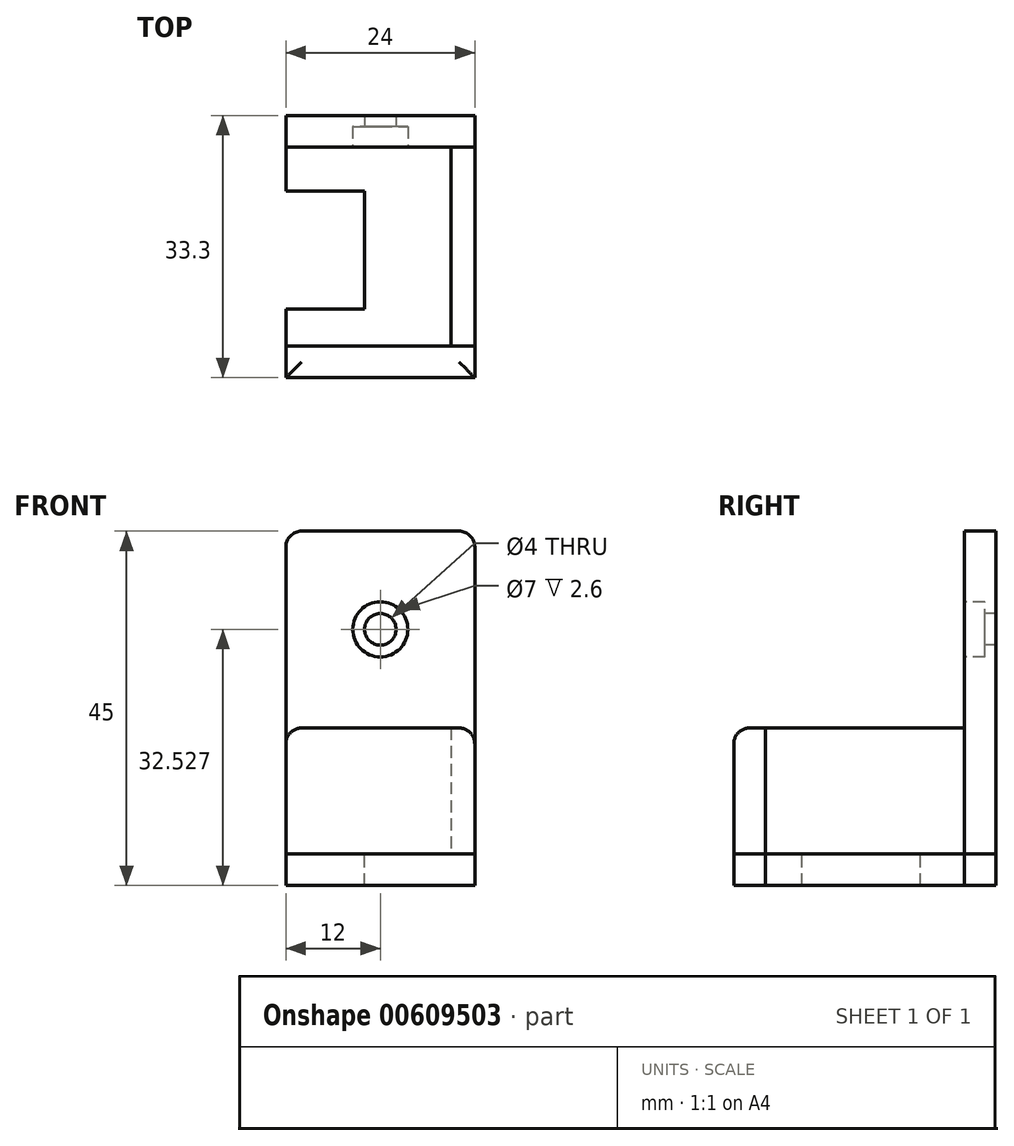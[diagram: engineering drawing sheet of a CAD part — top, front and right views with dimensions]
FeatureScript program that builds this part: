
annotation { "Feature Type Name" : "Feature", "Feature Type Description" : "" }
export const myFeature = defineFeature(function(context is Context, id is Id, definition is map)
    precondition{}
    {
        {
            var Q0;
            Q0=qCreatedBy(makeId("Top.planeOp"),FACE);
            var sketch = newSketch(context, id + "F0", { "sketchPlane" : qUnion([Q0])});
            skLineSegment(sketch, "E0.bottom", {"start": v(12, -16.65) * mm, "end": v(-12, -16.65) * mm});
            skLineSegment(sketch, "E0.top", {"start": v(12, 16.65) * mm, "end": v(-12, 16.65) * mm});
            skLineSegment(sketch, "E0.left", {"start": v(12, -16.65) * mm, "end": v(12, 16.65) * mm});
            skLineSegment(sketch, "E0.right", {"start": v(-12, -16.65) * mm, "end": v(-12, 16.65) * mm});
            skPoint(sketch, "E0.middle", {"position": v(0, 0) * mm});
            skSolve(sketch);
        }
        {
            var Q0;
            Q0=qSketchRegion(id+"F0",true);
            extrude(context, id + "F1", {"entities" : qUnion([Q0]), "depth" : 4 * mm, "offsetDistance" : 25 * mm});
        }
        {
            var Q0;
            Q0=makeQuery(id+"F0.imprint","IMPRINT",FACE,{"disambiguationData":[TD([[makeQuery(id+"F0.imprint","IMPRINT",EDGE,{"derivedFrom":sQuery(id+"F0.wireOp",EDGE,"E0.bottom")}),-1.0]])]});
            var sketch = newSketch(context, id + "F2", { "sketchPlane" : qUnion([Q0])});
            skLineSegment(sketch, "E1.bottom", {"start": v(-12, 16.65) * mm, "end": v(12, 16.65) * mm});
            skLineSegment(sketch, "E1.top", {"start": v(-12, 12.65) * mm, "end": v(12, 12.65) * mm});
            skLineSegment(sketch, "E1.left", {"start": v(-12, 16.65) * mm, "end": v(-12, 12.65) * mm});
            skLineSegment(sketch, "E1.right", {"start": v(12, 16.65) * mm, "end": v(12, 12.65) * mm});
            skSolve(sketch);
        }
        {
            var Q0;
            Q0=qSketchRegion(id+"F2",true);
            extrude(context, id + "F3", {"entities" : qUnion([Q0]), "depth" : 45 * mm, "offsetDistance" : 25 * mm});
        }
        {
            var Q0;
            Q0=makeQuery(id+"F2.imprint","IMPRINT",FACE,{"disambiguationData":[TD([[makeQuery(id+"F2.imprint","IMPRINT",EDGE,{"derivedFrom":sQuery(id+"F2.wireOp",EDGE,"E1.bottom")}),1.0]])]});
            var sketch = newSketch(context, id + "F4", { "sketchPlane" : qUnion([Q0])});
            skLineSegment(sketch, "E2.bottom", {"start": v(-12, -16.65) * mm, "end": v(12, -16.65) * mm});
            skLineSegment(sketch, "E2.top", {"start": v(-12, -12.65) * mm, "end": v(12, -12.65) * mm});
            skLineSegment(sketch, "E2.left", {"start": v(-12, -16.65) * mm, "end": v(-12, -12.65) * mm});
            skLineSegment(sketch, "E2.right", {"start": v(12, -16.65) * mm, "end": v(12, -12.65) * mm});
            skSolve(sketch);
        }
        {
            var Q0;
            Q0=qSketchRegion(id+"F4",true);
            extrude(context, id + "F5", {"entities" : qUnion([Q0]), "depth" : 20 * mm, "offsetDistance" : 25 * mm});
        }
        {
            var Q0;
            Q0=makeQuery(id+"F3.opExtrude","SWEPT_FACE",FACE,{"disambiguationData":[OSD([sQuery(id+"F2.wireOp",EDGE,"E1.top")])]});
            var sketch = newSketch(context, id + "F6", { "sketchPlane" : qUnion([Q0])});
            skCircle(sketch, "E3", {"center": v(0, 32.53) * mm, "radius": 2 * mm});
            skPoint(sketch, "E4", {"position": v(0, 40.1) * mm});
            skSolve(sketch);
        }
        {
            var Q0;
            Q0=qSketchRegion(id+"F6",true);
            extrude(context, id + "F7", {"entities" : qUnion([Q0]), "operationType" : NewBodyOperationType.REMOVE, "oppositeDirection" : true, "depth" : 6 * mm, "offsetDistance" : 25 * mm});
        }
        {
            var Q0;
            Q0=makeQuery(id+"F3.opExtrude","SWEPT_FACE",FACE,{"disambiguationData":[OSD([sQuery(id+"F2.wireOp",EDGE,"E1.top")])]});
            var sketch = newSketch(context, id + "F8", { "sketchPlane" : qUnion([Q0])});
            skCircle(sketch, "E5", {"center": v(0, 32.53) * mm, "radius": 3.5 * mm});
            skSolve(sketch);
        }
        {
            var Q0;
            Q0=qSketchRegion(id+"F8",true);
            extrude(context, id + "F9", {"entities" : qUnion([Q0]), "operationType" : NewBodyOperationType.REMOVE, "oppositeDirection" : true, "depth" : 2.6 * mm, "offsetDistance" : 25 * mm});
        }
        {
            var Q0;
            Q0=makeQuery(id+"F3.opExtrude","CAP_EDGE",EDGE,{"disambiguationData":[OSD([sQuery(id+"F2.wireOp",EDGE,"E1.left")])],"isStart":false});
            var Q1;
            Q1=makeQuery(id+"F3.opExtrude","CAP_EDGE",EDGE,{"disambiguationData":[OSD([sQuery(id+"F2.wireOp",EDGE,"E1.right")])],"isStart":false});
            fillet(context, id + "F10", {"entities" : qUnion([Q0, Q1]), "radius" : 2 * mm, "tangentPropagation" : true, "allowEdgeOverflow" : false});
        }
        {
            var Q0;
            Q0=makeQuery(id+"F1.opExtrude","CAP_FACE",FACE,{"disambiguationData":[OSD([sQuery(id+"F0.wireOp",EDGE,"E0.bottom"),sQuery(id+"F0.wireOp",EDGE,"E0.top"),sQuery(id+"F0.wireOp",EDGE,"E0.left"),sQuery(id+"F0.wireOp",EDGE,"E0.right")])],"isStart":false});
            var sketch = newSketch(context, id + "F11", { "sketchPlane" : qUnion([Q0])});
            skLineSegment(sketch, "E6.bottom", {"start": v(-17, 7.03) * mm, "end": v(-2, 7.03) * mm});
            skLineSegment(sketch, "E6.top", {"start": v(-17, -7.97) * mm, "end": v(-2, -7.97) * mm});
            skLineSegment(sketch, "E6.left", {"start": v(-17, 7.03) * mm, "end": v(-17, -7.97) * mm});
            skLineSegment(sketch, "E6.right", {"start": v(-2, 7.03) * mm, "end": v(-2, -7.97) * mm});
            skSolve(sketch);
        }
        {
            var Q0;
            Q0=makeQuery(id+"F1.opExtrude","CAP_FACE",FACE,{"disambiguationData":[OSD([sQuery(id+"F0.wireOp",EDGE,"E0.bottom"),sQuery(id+"F0.wireOp",EDGE,"E0.top"),sQuery(id+"F0.wireOp",EDGE,"E0.left"),sQuery(id+"F0.wireOp",EDGE,"E0.right")])],"isStart":false});
            var sketch = newSketch(context, id + "F12", { "sketchPlane" : qUnion([Q0])});
            skLineSegment(sketch, "E7.bottom", {"start": v(12, 12.65) * mm, "end": v(9, 12.65) * mm});
            skLineSegment(sketch, "E7.top", {"start": v(12, -12.65) * mm, "end": v(9, -12.65) * mm});
            skLineSegment(sketch, "E7.left", {"start": v(12, 12.65) * mm, "end": v(12, -12.65) * mm});
            skLineSegment(sketch, "E7.right", {"start": v(9, 12.65) * mm, "end": v(9, -12.65) * mm});
            skSolve(sketch);
        }
        {
            var Q0;
            Q0=makeQuery(id+"F12.imprint","IMPRINT",FACE,{"disambiguationData":[TD([[makeQuery(id+"F12.imprint","IMPRINT",EDGE,{"derivedFrom":sQuery(id+"F12.wireOp",EDGE,"E7.bottom")}),1.0]])]});
            extrude(context, id + "F13", {"entities" : qUnion([Q0]), "depth" : 16 * mm, "offsetDistance" : 25 * mm});
        }
        {
            var Q0;
            Q0=makeQuery(id+"F5.opExtrude","CAP_EDGE",EDGE,{"disambiguationData":[OSD([sQuery(id+"F4.wireOp",EDGE,"E2.bottom")])],"isStart":false});
            var Q1;
            Q1=makeQuery(id+"F5.opExtrude","CAP_EDGE",EDGE,{"disambiguationData":[OSD([sQuery(id+"F4.wireOp",EDGE,"E2.left")])],"isStart":false});
            var Q2;
            Q2=makeQuery(id+"F13.opExtrude","CAP_EDGE",EDGE,{"disambiguationData":[OSD([sQuery(id+"F12.wireOp",EDGE,"E7.left")])],"isStart":false});
            var Q3;
            Q3=makeQuery(id+"F5.opExtrude","CAP_EDGE",EDGE,{"disambiguationData":[OSD([sQuery(id+"F4.wireOp",EDGE,"E2.right")])],"isStart":false});
            fillet(context, id + "F14", {"entities" : qUnion([Q0, Q1, Q2, Q3]), "radius" : 2 * mm, "tangentPropagation" : true, "allowEdgeOverflow" : false});
        }
        {
            var Q0;
            Q0 = qSketchRegion(id + "F11", true);
            extrude(context, id + "F15", {"entities" : qUnion([Q0]), "operationType" : NewBodyOperationType.REMOVE, "oppositeDirection" : true, "depth" : 6 * mm, "offsetDistance" : 25 * mm});
        }
    });
